# Revit family: NaughtOne_Symbol45DegreeCurveWork
name_source: partatom
category: Furniture
units: mm (PartAtom-declared; Revit-internal decimal feet)

## family parameters
Always vertical = Yes
Cut with Voids When Loaded = No
Enable Cutting in Views = No
OmniClass Number = 23.40.20.00
OmniClass Title = General Furniture and Specialties
Render Appearance Source = Family Geometry
Room Calculation Point = No
Shared = Yes
Work Plane-Based = No

## types (5) — shared parameters
Assembly Code = E2020200
Manufacturer = Herman Miller, Inc.
Package Qty = 1
URL = http://www.hermanmiller.com
zero-valued in all types: Default Elevation

## per-type parameters (varying)
| type | 45 degree curve bench | 45 degree curve seat | Description | External 45 degree curve | Model | Type |
| 45 degree curve bench single fabric Work Ht | Yes | No | Symbol 45 Degree Curve 45 degree curve bench Work height 18 inch seat height single fabric | No | NOSYN510W1 | 1 |
| 45 degree curve seat single fabric Work Ht | No | Yes | Symbol 45 Degree Curve 45 degree curve seat Work height 18 inch seat height single fabric | No | NOSYN520W1 | 2 |
| 45 degree curve seat multi fabric Work Ht | No | Yes | Symbol 45 Degree Curve 45 degree curve seat Work height 18 inch seat height multi fabric | No | NOSYN520W2 | 3 |
| External 45 degree curve seat single fabric Work Ht | No | No | Symbol 45 Degree Curve External 45 degree curve seat Work height 18 inch seat height single fabric | Yes | NOSYN530W1 | 4 |
| External 45 degree curve seat multi fabric Work Ht | No | No | Symbol 45 Degree Curve External 45 degree curve seat Work height 18 inch seat height multi fabric | Yes | NOSYN530W2 | 5 |

## geometry (parser evidence)
native form markers: Sweep x6
no freeform markers — native parametric forms only
